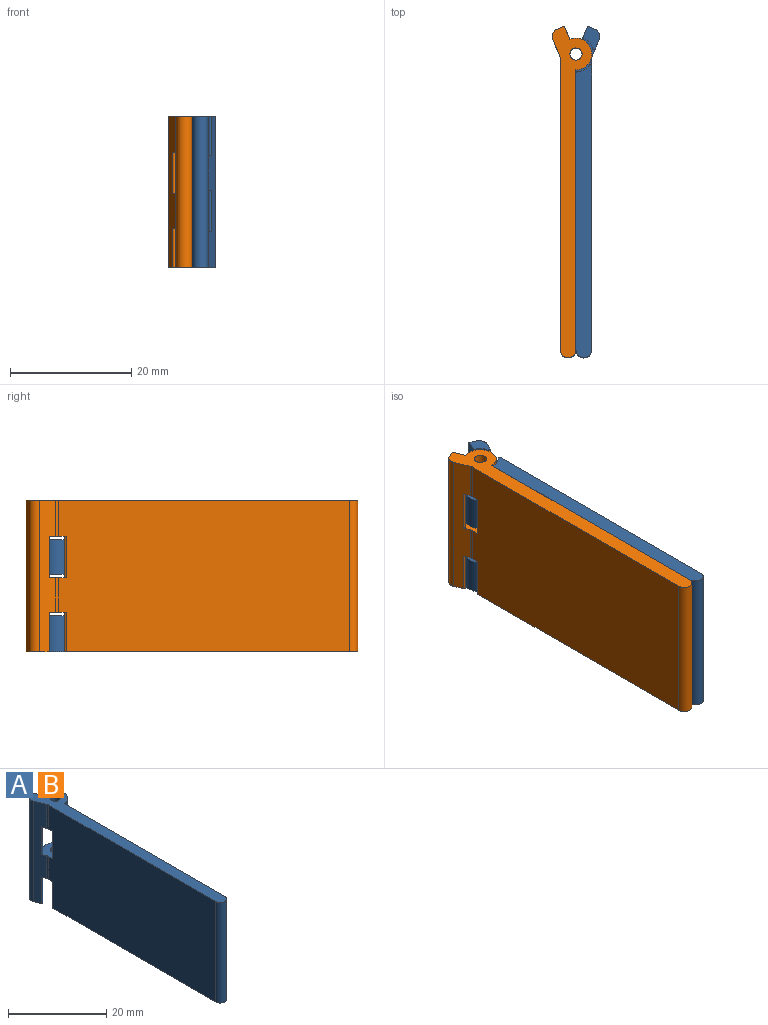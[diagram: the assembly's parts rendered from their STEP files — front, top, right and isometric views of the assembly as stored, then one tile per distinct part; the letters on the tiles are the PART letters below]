
ASSEMBLY  parts=2 mates=1
PART A: 31 faces, bbox 6.5x54.6x25 mm
  f0: cylinder r=2.6mm len=5.65mm, axis (0,0,-1), area 51.9mm2, adj f5,f7,f11,f17
  f1: plane 48.24x2.6mm, normal (0,0,-1), area 122.8mm2, adj f4,f5,f13,f23,f24,f30
  f2: plane 25x1.2mm, normal (-0.38,0.92,0), area 32.5mm2, adj f7,f9,f10,f28
  f3: plane 25x2.7mm, normal (-0.92,-0.38,0), area 57.2mm2, adj f9,f10,f11,f16,f17,f19,f25,f27
  f4: plane 47.92x25mm, normal (-1,0,0), area 1182.2mm2, adj f1,f9,f11,f16,f17,f20,f23,f27
  f5: plane 46.1x25mm, normal (1,0,0), area 1145.9mm2, adj f0,f1,f6,f9,f11,f16,f17,f21
  f6: cylinder r=2.6mm len=5.95mm, axis (0,0,-1), area 54.7mm2, adj f5,f7,f9,f16
  f7: plane 25x2.22mm, normal (0.92,0.38,0), area 53.4mm2, adj f0,f2,f6,f9,f10,f11,f16,f17
  f8: cylinder r=1mm len=5.95mm, axis (0,0,-1), area 37.4mm2, adj f9,f16
  f9: plane 54.62x6.52mm, normal (0,0,1), area 149.4mm2, adj f2,f3,f4,f5,f6,f7,f8,f28
  f10: plane 3.93x2.75mm, normal (0,0,-1), area 6.2mm2, adj f2,f3,f7,f12,f25,f26,f28
  f11: plane 5.95x5.75mm, normal (0,0,-1), area 20.3mm2, adj f0,f3,f4,f5,f7,f12,f13,f14
  f12: cylinder r=2.9mm len=6.55mm, axis (0,0,-1), area 15.6mm2, adj f10,f11,f25,f26
  f13: cylinder r=2.9mm len=6.55mm, axis (0,0,-1), area 15.6mm2, adj f1,f11,f23,f24
  f14: cylinder r=1mm len=5.65mm, axis (0,0,-1), area 35.5mm2, adj f11,f17
  f15: cylinder r=2.9mm len=6.85mm, axis (0,0,-1), area 16.3mm2, adj f16,f17,f19,f22
  f16: plane 5.95x5.75mm, normal (0,0,-1), area 20.3mm2, adj f3,f4,f5,f6,f7,f8,f15,f18
  f17: plane 5.95x5.75mm, normal (0,0,1), area 20.3mm2, adj f0,f3,f4,f5,f7,f14,f15,f18
  f18: cylinder r=2.9mm len=6.85mm, axis (0,0,-1), area 16.3mm2, adj f16,f17,f20,f21
  f19: cylinder r=0.2mm len=6.85mm, axis (0,0,-1), area 3.4mm2, adj f3,f15,f16,f17
  f20: cylinder r=0.2mm len=6.85mm, axis (0,0,-1), area 3.4mm2, adj f4,f16,f17,f18
  f21: cylinder r=0.2mm len=6.85mm, axis (0,0,-1), area 2.1mm2, adj f5,f16,f17,f18
  f22: cylinder r=0.2mm len=6.85mm, axis (0,0,-1), area 2.1mm2, adj f7,f15,f16,f17
  f23: cylinder r=0.2mm len=6.55mm, axis (0,0,-1), area 3.2mm2, adj f1,f4,f11,f13
  f24: cylinder r=0.2mm len=6.55mm, axis (0,0,-1), area 2mm2, adj f1,f5,f11,f13
  f25: cylinder r=0.2mm len=6.55mm, axis (0,0,-1), area 3.2mm2, adj f3,f10,f11,f12
  f26: cylinder r=0.2mm len=6.55mm, axis (0,0,-1), area 2mm2, adj f7,f10,f11,f12
  f27: cylinder r=1.3mm len=5.65mm, axis (0,0,-1), area 2.9mm2, adj f3,f4,f11,f17
  f28: cylinder r=1.3mm len=25mm, axis (0,0,-1), area 51.1mm2, adj f2,f3,f9,f10
  f29: cylinder r=1.3mm len=5.95mm, axis (0,0,-1), area 3mm2, adj f3,f4,f9,f16
  f30: cylinder r=1.3mm len=25mm, axis (0,0,-1), area 102.1mm2, adj f1,f4,f5,f9
PART B: same geometry as A
PLACE A rot(axis=(0,1,0),180deg) t=(14.34,52.56,7.71)mm
PLACE B t=(14.34,52.56,-17.29)mm
MATE revolute A.f0 <-> B.f0  axis (0,0,1) through (14.34,52.56,7.71)mm
